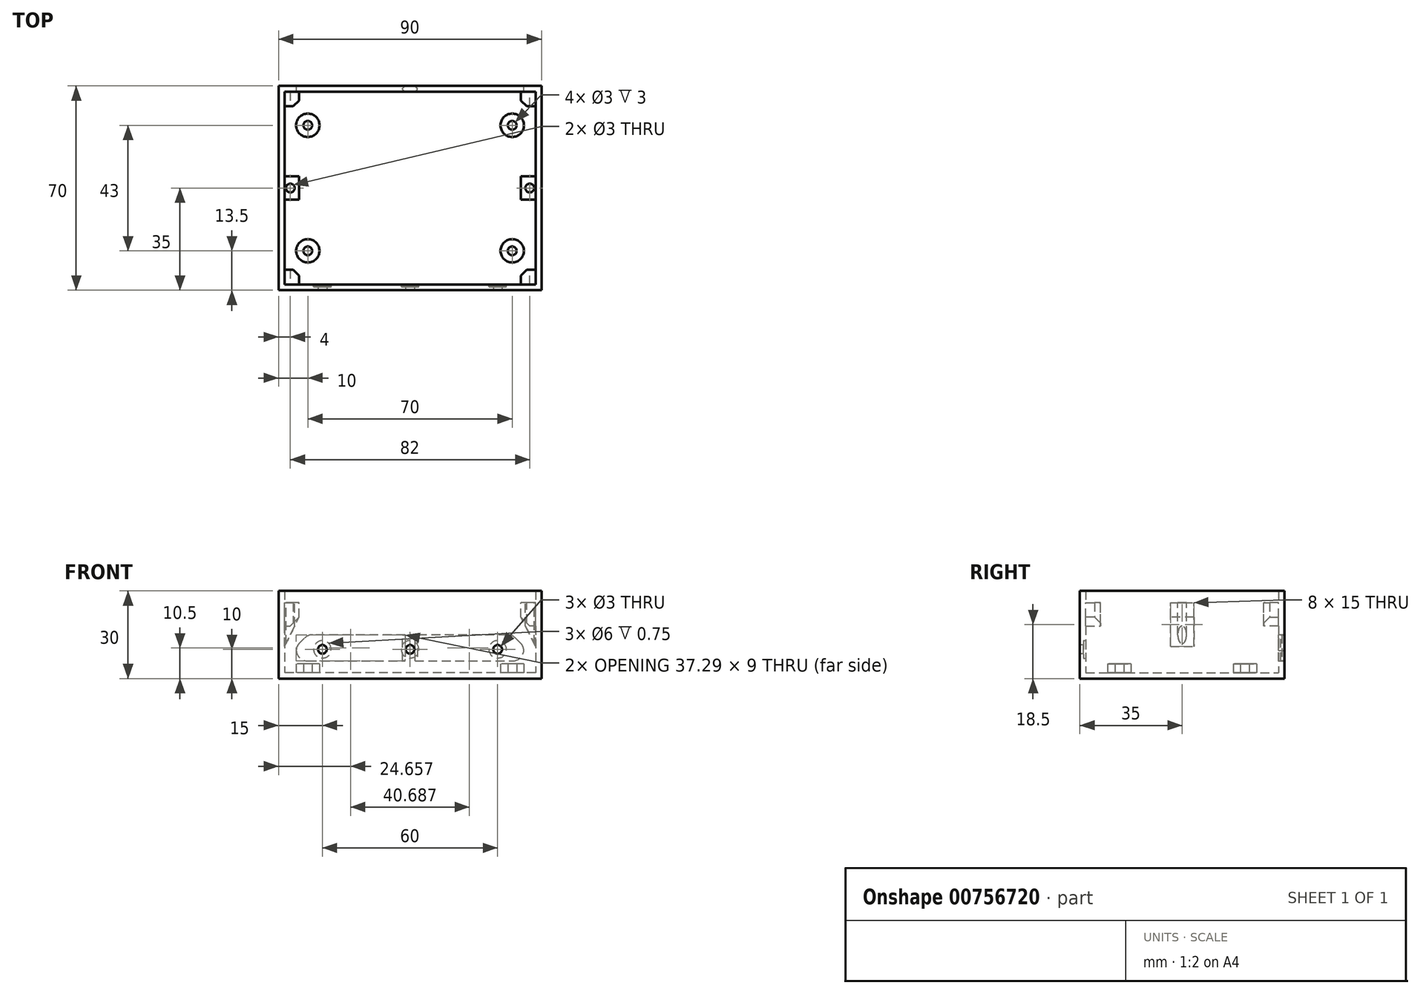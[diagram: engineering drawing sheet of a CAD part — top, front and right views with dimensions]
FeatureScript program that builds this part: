
annotation { "Feature Type Name" : "Feature", "Feature Type Description" : "" }
export const myFeature = defineFeature(function(context is Context, id is Id, definition is map)
    precondition{}
    {
        {
            var Q0;
            Q0=qCreatedBy(makeId("Top.planeOp"),FACE);
            var sketch = newSketch(context, id + "F0", { "sketchPlane" : qUnion([Q0])});
            skLineSegment(sketch, "E0.bottom", {"start": v(38.25, -25) * mm, "end": v(-38.25, -25) * mm, "construction": true});
            skLineSegment(sketch, "E0.top", {"start": v(38.25, 25) * mm, "end": v(-38.25, 25) * mm, "construction": true});
            skLineSegment(sketch, "E0.left", {"start": v(38.25, -25) * mm, "end": v(38.25, 25) * mm, "construction": true});
            skLineSegment(sketch, "E0.right", {"start": v(-38.25, -25) * mm, "end": v(-38.25, 25) * mm, "construction": true});
            skPoint(sketch, "E0.middle", {"position": v(0, 0) * mm});
            skPoint(sketch, "E1", {"position": v(35, 21.5) * mm});
            skPoint(sketch, "E2", {"position": v(-35, 21.5) * mm});
            skPoint(sketch, "E3", {"position": v(-35, -21.5) * mm});
            skPoint(sketch, "E4", {"position": v(35, -21.5) * mm});
            skLineSegment(sketch, "E5", {"start": v(35, 21.5) * mm, "end": v(-35, 21.5) * mm, "construction": true});
            skLineSegment(sketch, "E6", {"start": v(-35, -21.5) * mm, "end": v(35, -21.5) * mm, "construction": true});
            skLineSegment(sketch, "E7", {"start": v(35, 21.5) * mm, "end": v(35, -21.5) * mm, "construction": true});
            skLineSegment(sketch, "E8", {"start": v(-35, 21.5) * mm, "end": v(-35, -21.5) * mm, "construction": true});
            skCircle(sketch, "E9", {"center": v(-35, 21.5) * mm, "radius": 1.5 * mm});
            skCircle(sketch, "E10", {"center": v(35, 21.5) * mm, "radius": 1.5 * mm});
            skCircle(sketch, "E11", {"center": v(35, -21.5) * mm, "radius": 1.5 * mm});
            skCircle(sketch, "E12", {"center": v(-35, -21.5) * mm, "radius": 1.5 * mm});
            skLineSegment(sketch, "E13.bottom", {"start": v(45, -35) * mm, "end": v(-45, -35) * mm});
            skLineSegment(sketch, "E13.top", {"start": v(45, 35) * mm, "end": v(-45, 35) * mm});
            skLineSegment(sketch, "E13.left", {"start": v(45, -35) * mm, "end": v(45, 35) * mm});
            skLineSegment(sketch, "E13.right", {"start": v(-45, -35) * mm, "end": v(-45, 35) * mm});
            skLineSegment(sketch, "E14.bottom", {"start": v(43, -33) * mm, "end": v(-43, -33) * mm});
            skLineSegment(sketch, "E14.top", {"start": v(43, 33) * mm, "end": v(-43, 33) * mm});
            skLineSegment(sketch, "E14.left", {"start": v(43, -33) * mm, "end": v(43, 33) * mm});
            skLineSegment(sketch, "E14.right", {"start": v(-43, -33) * mm, "end": v(-43, 33) * mm});
            skCircle(sketch, "E15", {"center": v(-35, 21.5) * mm, "radius": 4 * mm});
            skCircle(sketch, "E16", {"center": v(35, 21.5) * mm, "radius": 4 * mm});
            skCircle(sketch, "E17", {"center": v(35, -21.5) * mm, "radius": 4 * mm});
            skCircle(sketch, "E18", {"center": v(-35, -21.5) * mm, "radius": 4 * mm});
            skSolve(sketch);
        }
        {
            var Q0;
            Q0=makeQuery(id+"F0.imprint","IMPRINT",FACE,{"disambiguationData":[TD([[makeQuery(id+"F0.imprint","IMPRINT",EDGE,{"derivedFrom":sQuery(id+"F0.wireOp",EDGE,"E9")}),-1.0]])]});
            var Q1;
            Q1=makeQuery(id+"F0.imprint","IMPRINT",FACE,{"disambiguationData":[TD([[makeQuery(id+"F0.imprint","IMPRINT",EDGE,{"derivedFrom":sQuery(id+"F0.wireOp",EDGE,"E10")}),-1.0]])]});
            var Q2;
            Q2=makeQuery(id+"F0.imprint","IMPRINT",FACE,{"disambiguationData":[TD([[makeQuery(id+"F0.imprint","IMPRINT",EDGE,{"derivedFrom":sQuery(id+"F0.wireOp",EDGE,"E11")}),-1.0]])]});
            var Q3;
            Q3=makeQuery(id+"F0.imprint","IMPRINT",FACE,{"disambiguationData":[TD([[makeQuery(id+"F0.imprint","IMPRINT",EDGE,{"derivedFrom":sQuery(id+"F0.wireOp",EDGE,"E12")}),-1.0]])]});
            extrude(context, id + "F1", {"entities" : qUnion([Q0, Q1, Q2, Q3]), "depth" : 5 * mm, "offsetDistance" : 25 * mm});
        }
        {
            var Q0;
            Q0=makeQuery(id+"F0.imprint","IMPRINT",FACE,{"disambiguationData":[TD([[makeQuery(id+"F0.imprint","IMPRINT",EDGE,{"derivedFrom":sQuery(id+"F0.wireOp",EDGE,"E9")}),-1.0]])]});
            var Q1;
            Q1=makeQuery(id+"F0.imprint","IMPRINT",FACE,{"disambiguationData":[TD([[makeQuery(id+"F0.imprint","IMPRINT",EDGE,{"derivedFrom":sQuery(id+"F0.wireOp",EDGE,"E14.bottom")}),-1.0]])]});
            var Q2;
            Q2=makeQuery(id+"F0.imprint","IMPRINT",FACE,{"disambiguationData":[TD([[makeQuery(id+"F0.imprint","IMPRINT",EDGE,{"derivedFrom":sQuery(id+"F0.wireOp",EDGE,"E10")}),1.0]])]});
            var Q3;
            Q3=makeQuery(id+"F0.imprint","IMPRINT",FACE,{"disambiguationData":[TD([[makeQuery(id+"F0.imprint","IMPRINT",EDGE,{"derivedFrom":sQuery(id+"F0.wireOp",EDGE,"E11")}),1.0]])]});
            var Q4;
            Q4=makeQuery(id+"F0.imprint","IMPRINT",FACE,{"disambiguationData":[TD([[makeQuery(id+"F0.imprint","IMPRINT",EDGE,{"derivedFrom":sQuery(id+"F0.wireOp",EDGE,"E12")}),1.0]])]});
            var Q5;
            Q5=makeQuery(id+"F0.imprint","IMPRINT",FACE,{"disambiguationData":[TD([[makeQuery(id+"F0.imprint","IMPRINT",EDGE,{"derivedFrom":sQuery(id+"F0.wireOp",EDGE,"E9")}),1.0]])]});
            extrude(context, id + "F2", {"entities" : qUnion([Q0, Q1, Q2, Q3, Q4, Q5]), "operationType" : NewBodyOperationType.ADD, "depth" : 2 * mm, "offsetDistance" : 25 * mm});
        }
        {
            var Q0;
            Q0=makeQuery(id+"F0.imprint","IMPRINT",FACE,{"disambiguationData":[TD([[makeQuery(id+"F0.imprint","IMPRINT",EDGE,{"derivedFrom":sQuery(id+"F0.wireOp",EDGE,"E13.bottom")}),-1.0]])]});
            extrude(context, id + "F3", {"entities" : qUnion([Q0]), "operationType" : NewBodyOperationType.ADD, "depth" : 30 * mm, "offsetDistance" : 25 * mm});
        }
        {
            var Q0;
            Q0=makeQuery(id+"F3.opExtrude","SWEPT_FACE",FACE,{"disambiguationData":[OSD([sQuery(id+"F0.wireOp",EDGE,"E13.bottom")])]});
            var sketch = newSketch(context, id + "F4", { "sketchPlane" : qUnion([Q0])});
            skLineSegment(sketch, "E19", {"start": v(-45, 10) * mm, "end": v(45, 10) * mm, "construction": true});
            skCircle(sketch, "E20", {"center": v(-30, 10) * mm, "radius": 1.5 * mm});
            skCircle(sketch, "E21.1.0.0", {"center": v(0, 10) * mm, "radius": 1.5 * mm});
            skCircle(sketch, "E21.2.0.0", {"center": v(30, 10) * mm, "radius": 1.5 * mm});
            skLineSegment(sketch, "E21.direction1", {"start": v(-30, 10) * mm, "end": v(0, 10) * mm, "construction": true});
            skCircle(sketch, "E22", {"center": v(-30, 10) * mm, "radius": 3 * mm});
            skCircle(sketch, "E23.1.0.0", {"center": v(0, 10) * mm, "radius": 3 * mm});
            skCircle(sketch, "E23.2.0.0", {"center": v(30, 10) * mm, "radius": 3 * mm});
            skSolve(sketch);
        }
        {
            var Q0;
            Q0=makeQuery(id+"F4.imprint","IMPRINT",FACE,{"disambiguationData":[TD([[makeQuery(id+"F4.imprint","IMPRINT",EDGE,{"derivedFrom":sQuery(id+"F4.wireOp",EDGE,"E20")}),1.0]])]});
            var Q1;
            Q1=makeQuery(id+"F4.imprint","IMPRINT",FACE,{"disambiguationData":[TD([[makeQuery(id+"F4.imprint","IMPRINT",EDGE,{"derivedFrom":sQuery(id+"F4.wireOp",EDGE,"E21.1.0.0")}),1.0]])]});
            var Q2;
            Q2=makeQuery(id+"F4.imprint","IMPRINT",FACE,{"disambiguationData":[TD([[makeQuery(id+"F4.imprint","IMPRINT",EDGE,{"derivedFrom":sQuery(id+"F4.wireOp",EDGE,"E21.2.0.0")}),1.0]])]});
            extrude(context, id + "F5", {"entities" : qUnion([Q0, Q1, Q2]), "operationType" : NewBodyOperationType.REMOVE, "endBound" : BoundingType.UP_TO_NEXT, "oppositeDirection" : true, "depth" : 25 * mm, "offsetDistance" : 25 * mm});
        }
        {
            var Q0;
            Q0=makeQuery(id+"F3.opExtrude","SWEPT_FACE",FACE,{"disambiguationData":[OSD([sQuery(id+"F0.wireOp",EDGE,"E14.bottom")])]});
            var sketch = newSketch(context, id + "F6", { "sketchPlane" : qUnion([Q0])});
            skCircle(sketch, "E24", {"center": v(-30, 10) * mm, "radius": 3 * mm});
            skCircle(sketch, "E25.1.0.0", {"center": v(0, 10) * mm, "radius": 3 * mm});
            skCircle(sketch, "E25.2.0.0", {"center": v(30, 10) * mm, "radius": 3 * mm});
            skLineSegment(sketch, "E25.direction1", {"start": v(-30, 10) * mm, "end": v(0, 10) * mm, "construction": true});
            skSolve(sketch);
        }
        {
            var Q0;
            Q0=makeQuery(id+"F6.imprint","IMPRINT",FACE,{"disambiguationData":[TD([[makeQuery(id+"F6.imprint","IMPRINT",EDGE,{"derivedFrom":sQuery(id+"F6.wireOp",EDGE,"E24")}),1.0]])]});
            var Q1;
            Q1=makeQuery(id+"F6.imprint","IMPRINT",FACE,{"disambiguationData":[TD([[makeQuery(id+"F6.imprint","IMPRINT",EDGE,{"derivedFrom":sQuery(id+"F6.wireOp",EDGE,"E25.1.0.0")}),1.0]])]});
            var Q2;
            Q2=makeQuery(id+"F6.imprint","IMPRINT",FACE,{"disambiguationData":[TD([[makeQuery(id+"F6.imprint","IMPRINT",EDGE,{"derivedFrom":sQuery(id+"F6.wireOp",EDGE,"E25.2.0.0")}),1.0]])]});
            extrude(context, id + "F7", {"entities" : qUnion([Q0, Q1, Q2]), "operationType" : NewBodyOperationType.REMOVE, "oppositeDirection" : true, "depth" : 0.75 * mm, "offsetDistance" : 25 * mm});
        }
        {
            var Q0;
            Q0=makeQuery(id+"F3.opExtrude","CAP_FACE",FACE,{"disambiguationData":[OSD([sQuery(id+"F0.wireOp",EDGE,"E13.bottom"),sQuery(id+"F0.wireOp",EDGE,"E13.top"),sQuery(id+"F0.wireOp",EDGE,"E13.left"),sQuery(id+"F0.wireOp",EDGE,"E13.right"),sQuery(id+"F0.wireOp",EDGE,"E14.bottom"),sQuery(id+"F0.wireOp",EDGE,"E14.top"),sQuery(id+"F0.wireOp",EDGE,"E14.left"),sQuery(id+"F0.wireOp",EDGE,"E14.right")])],"isStart":false});
            cPlane(context, id + "F8", {"entities" : qUnion([Q0]), "cplaneType" : CPlaneType.OFFSET, "offset" : 4 * mm, "oppositeDirection" : true, "width" : 150 * mm, "height" : 150 * mm});
        }
        {
            var Q0;
            Q0=qCreatedBy(id+"F8.planeOp",FACE);
            var sketch = newSketch(context, id + "F9", { "sketchPlane" : qUnion([Q0])});
            skLineSegment(sketch, "E26.bottom", {"start": v(43, -33) * mm, "end": v(38, -33) * mm});
            skLineSegment(sketch, "E26.top", {"start": v(43, -28) * mm, "end": v(38, -28) * mm});
            skLineSegment(sketch, "E26.left", {"start": v(43, -33) * mm, "end": v(43, -28) * mm});
            skLineSegment(sketch, "E26.right", {"start": v(38, -33) * mm, "end": v(38, -28) * mm});
            skLineSegment(sketch, "E27.bottom", {"start": v(-43, -33) * mm, "end": v(-38, -33) * mm});
            skLineSegment(sketch, "E27.top", {"start": v(-43, -28) * mm, "end": v(-38, -28) * mm});
            skLineSegment(sketch, "E27.left", {"start": v(-43, -33) * mm, "end": v(-43, -28) * mm});
            skLineSegment(sketch, "E27.right", {"start": v(-38, -33) * mm, "end": v(-38, -28) * mm});
            skLineSegment(sketch, "E28.bottom", {"start": v(-43, 33) * mm, "end": v(-38, 33) * mm});
            skLineSegment(sketch, "E28.top", {"start": v(-43, 28) * mm, "end": v(-38, 28) * mm});
            skLineSegment(sketch, "E28.left", {"start": v(-43, 33) * mm, "end": v(-43, 28) * mm});
            skLineSegment(sketch, "E28.right", {"start": v(-38, 33) * mm, "end": v(-38, 28) * mm});
            skLineSegment(sketch, "E29.bottom", {"start": v(43, 33) * mm, "end": v(38, 33) * mm});
            skLineSegment(sketch, "E29.top", {"start": v(43, 28) * mm, "end": v(38, 28) * mm});
            skLineSegment(sketch, "E29.left", {"start": v(43, 33) * mm, "end": v(43, 28) * mm});
            skLineSegment(sketch, "E29.right", {"start": v(38, 33) * mm, "end": v(38, 28) * mm});
            skLineSegment(sketch, "E30", {"start": v(-43, 0) * mm, "end": v(43, 0) * mm, "construction": true});
            skLineSegment(sketch, "E31.bottom", {"start": v(43, -4) * mm, "end": v(38, -4) * mm});
            skLineSegment(sketch, "E31.top", {"start": v(43, 4) * mm, "end": v(38, 4) * mm});
            skLineSegment(sketch, "E31.left", {"start": v(43, -4) * mm, "end": v(43, 4) * mm});
            skLineSegment(sketch, "E31.right", {"start": v(38, -4) * mm, "end": v(38, 4) * mm});
            skLineSegment(sketch, "E32.bottom", {"start": v(-43, -4) * mm, "end": v(-38, -4) * mm});
            skLineSegment(sketch, "E32.top", {"start": v(-43, 4) * mm, "end": v(-38, 4) * mm});
            skLineSegment(sketch, "E32.left", {"start": v(-43, -4) * mm, "end": v(-43, 4) * mm});
            skLineSegment(sketch, "E32.right", {"start": v(-38, -4) * mm, "end": v(-38, 4) * mm});
            skPoint(sketch, "E33", {"position": v(43, 0) * mm});
            skPoint(sketch, "E34", {"position": v(-43, 0) * mm});
            skPoint(sketch, "E35", {"position": v(41, 0) * mm});
            skPoint(sketch, "E36", {"position": v(-41, 0) * mm});
            skCircle(sketch, "E37", {"center": v(41, 0) * mm, "radius": 1.5 * mm});
            skCircle(sketch, "E38", {"center": v(-41, 0) * mm, "radius": 1.5 * mm});
            skSolve(sketch);
        }
        {
            var Q0;
            Q0=makeQuery(id+"F9.imprint","IMPRINT",FACE,{"disambiguationData":[TD([[makeQuery(id+"F9.imprint","IMPRINT",EDGE,{"derivedFrom":sQuery(id+"F9.wireOp",EDGE,"E26.bottom")}),-1.0]])]});
            var Q1;
            Q1=makeQuery(id+"F9.imprint","IMPRINT",FACE,{"disambiguationData":[TD([[makeQuery(id+"F9.imprint","IMPRINT",EDGE,{"derivedFrom":sQuery(id+"F9.wireOp",EDGE,"E29.bottom")}),1.0]])]});
            var Q2;
            Q2=makeQuery(id+"F9.imprint","IMPRINT",FACE,{"disambiguationData":[TD([[makeQuery(id+"F9.imprint","IMPRINT",EDGE,{"derivedFrom":sQuery(id+"F9.wireOp",EDGE,"E27.bottom")}),1.0]])]});
            var Q3;
            Q3=makeQuery(id+"F9.imprint","IMPRINT",FACE,{"disambiguationData":[TD([[makeQuery(id+"F9.imprint","IMPRINT",EDGE,{"derivedFrom":sQuery(id+"F9.wireOp",EDGE,"E28.bottom")}),-1.0]])]});
            extrude(context, id + "F10", {"entities" : qUnion([Q0, Q1, Q2, Q3]), "operationType" : NewBodyOperationType.ADD, "oppositeDirection" : true, "depth" : 8 * mm, "offsetDistance" : 25 * mm});
        }
        {
            var Q0;
            Q0=makeQuery(id+"F10.opExtrude","CAP_EDGE",EDGE,{"disambiguationData":[OSD([sQuery(id+"F9.wireOp",EDGE,"E27.right")])],"isStart":false});
            var Q1;
            Q1=makeQuery(id+"F10.opExtrude","CAP_EDGE",EDGE,{"disambiguationData":[OSD([sQuery(id+"F9.wireOp",EDGE,"E28.right")])],"isStart":false});
            var Q2;
            Q2=makeQuery(id+"F10.opExtrude","CAP_EDGE",EDGE,{"disambiguationData":[OSD([sQuery(id+"F9.wireOp",EDGE,"E26.right")])],"isStart":false});
            var Q3;
            Q3=makeQuery(id+"F10.opExtrude","CAP_EDGE",EDGE,{"disambiguationData":[OSD([sQuery(id+"F9.wireOp",EDGE,"E29.right")])],"isStart":false});
            chamfer(context, id + "F11", {"entities" : qUnion([Q0, Q1, Q2, Q3]), "width" : 3 * mm, "tangentPropagation" : true});
        }
        {
            var Q0;
            Q0=makeQuery(id+"F10.opExtrude","SWEPT_EDGE",EDGE,{"disambiguationData":[OSD([sQuery(id+"F9.wireOp",EDGE,"E28.top"),sQuery(id+"F9.wireOp",EDGE,"E28.right")])]});
            var Q1;
            Q1=makeQuery(id+"F10.opExtrude","SWEPT_EDGE",EDGE,{"disambiguationData":[OSD([sQuery(id+"F9.wireOp",EDGE,"E27.top"),sQuery(id+"F9.wireOp",EDGE,"E27.right")])]});
            var Q2;
            Q2=makeQuery(id+"F10.opExtrude","SWEPT_EDGE",EDGE,{"disambiguationData":[OSD([sQuery(id+"F9.wireOp",EDGE,"E26.top"),sQuery(id+"F9.wireOp",EDGE,"E26.right")])]});
            var Q3;
            Q3=makeQuery(id+"F10.opExtrude","SWEPT_EDGE",EDGE,{"disambiguationData":[OSD([sQuery(id+"F9.wireOp",EDGE,"E29.top"),sQuery(id+"F9.wireOp",EDGE,"E29.right")])]});
            chamfer(context, id + "F12", {"entities" : qUnion([Q0, Q1, Q2, Q3]), "width" : 2 * mm, "tangentPropagation" : true});
        }
        {
            var Q0;
            Q0=makeQuery(id+"F3.opExtrude","SWEPT_FACE",FACE,{"disambiguationData":[OSD([sQuery(id+"F0.wireOp",EDGE,"E13.top")])]});
            var sketch = newSketch(context, id + "F13", { "sketchPlane" : qUnion([Q0])});
            skLineSegment(sketch, "E39", {"start": v(-45, 15) * mm, "end": v(45, 15) * mm});
            skLineSegment(sketch, "E40", {"start": v(45, 6) * mm, "end": v(-45, 6) * mm});
            skLineSegment(sketch, "E41", {"start": v(39, 15) * mm, "end": v(39, 6) * mm});
            skLineSegment(sketch, "E42", {"start": v(-39, 15) * mm, "end": v(-39, 6) * mm});
            skSolve(sketch);
        }
        {
            var Q0;
            {var subQ0=sQuery(id+"F13.wireOp",EDGE,"E41");Q0=makeQuery(id+"F13.imprint","IMPRINT",FACE,{"disambiguationData":[TD([[makeQuery(id+"F13.imprint","IMPRINT",EDGE,{"derivedFrom":subQ0}),-1.0]])]});}
            extrude(context, id + "F14", {"entities" : qUnion([Q0]), "operationType" : NewBodyOperationType.REMOVE, "endBound" : BoundingType.UP_TO_NEXT, "oppositeDirection" : true, "depth" : 25 * mm, "offsetDistance" : 25 * mm});
        }
        {
            var Q0;
            Q0=makeQuery(id+"F14.boolean.opBoolean","COPY",EDGE,{"derivedFrom":makeQuery(id+"F14.opExtrude","SWEPT_EDGE",EDGE,{"disambiguationData":[OSD([sQuery(id+"F13.wireOp",EDGE,"E39"),sQuery(id+"F13.wireOp",EDGE,"E41")])]})});
            var Q1;
            Q1=makeQuery(id+"F14.boolean.opBoolean","COPY",EDGE,{"derivedFrom":makeQuery(id+"F14.opExtrude","SWEPT_EDGE",EDGE,{"disambiguationData":[OSD([sQuery(id+"F13.wireOp",EDGE,"E39"),sQuery(id+"F13.wireOp",EDGE,"E42")])]})});
            chamfer(context, id + "F15", {"entities" : qUnion([Q0, Q1]), "width" : 4 * mm, "tangentPropagation" : true});
        }
        {
            var Q0;
            Q0=makeQuery(id+"F14.boolean.opBoolean","COPY",EDGE,{"derivedFrom":makeQuery(id+"F14.opExtrude","SWEPT_EDGE",EDGE,{"disambiguationData":[OSD([sQuery(id+"F13.wireOp",EDGE,"E40"),sQuery(id+"F13.wireOp",EDGE,"E41")])]})});
            var Q1;
            Q1=makeQuery(id+"F14.boolean.opBoolean","COPY",EDGE,{"derivedFrom":makeQuery(id+"F14.opExtrude","SWEPT_EDGE",EDGE,{"disambiguationData":[OSD([sQuery(id+"F13.wireOp",EDGE,"E40"),sQuery(id+"F13.wireOp",EDGE,"E42")])]})});
            var Q2;
            {var subQ0=sQuery(id+"F13.wireOp",EDGE,"E39");Q2=makeQuery(id+"F15.opChamfer","BLEND_EDGE",EDGE,{"blendedFrom":[makeQuery(id+"F14.boolean.opBoolean","COPY",EDGE,{"derivedFrom":makeQuery(id+"F14.opExtrude","SWEPT_EDGE",EDGE,{"disambiguationData":[OSD([subQ0,sQuery(id+"F13.wireOp",EDGE,"E41")])]})}),makeQuery(id+"F14.boolean.opBoolean","COPY",FACE,{"derivedFrom":makeQuery(id+"F14.opExtrude","SWEPT_FACE",FACE,{"disambiguationData":[OSD([subQ0])]})})],"blendedInto":[makeQuery(id+"F14.boolean.opBoolean","COPY",FACE,{"derivedFrom":makeQuery(id+"F14.opExtrude","SWEPT_FACE",FACE,{"disambiguationData":[OSD([subQ0])]})})]});}
            var Q3;
            {var subQ0=sQuery(id+"F13.wireOp",EDGE,"E39");Q3=makeQuery(id+"F15.opChamfer","BLEND_EDGE",EDGE,{"blendedFrom":[makeQuery(id+"F14.boolean.opBoolean","COPY",EDGE,{"derivedFrom":makeQuery(id+"F14.opExtrude","SWEPT_EDGE",EDGE,{"disambiguationData":[OSD([subQ0,sQuery(id+"F13.wireOp",EDGE,"E42")])]})}),makeQuery(id+"F14.boolean.opBoolean","COPY",FACE,{"derivedFrom":makeQuery(id+"F14.opExtrude","SWEPT_FACE",FACE,{"disambiguationData":[OSD([subQ0])]})})],"blendedInto":[makeQuery(id+"F14.boolean.opBoolean","COPY",FACE,{"derivedFrom":makeQuery(id+"F14.opExtrude","SWEPT_FACE",FACE,{"disambiguationData":[OSD([subQ0])]})})]});}
            var Q4;
            {var subQ0=sQuery(id+"F13.wireOp",EDGE,"E41");Q4=makeQuery(id+"F15.opChamfer","BLEND_EDGE",EDGE,{"blendedFrom":[makeQuery(id+"F14.boolean.opBoolean","COPY",EDGE,{"derivedFrom":makeQuery(id+"F14.opExtrude","SWEPT_EDGE",EDGE,{"disambiguationData":[OSD([sQuery(id+"F13.wireOp",EDGE,"E39"),subQ0])]})}),makeQuery(id+"F14.boolean.opBoolean","COPY",FACE,{"derivedFrom":makeQuery(id+"F14.opExtrude","SWEPT_FACE",FACE,{"disambiguationData":[OSD([subQ0])]})})],"blendedInto":[makeQuery(id+"F14.boolean.opBoolean","COPY",FACE,{"derivedFrom":makeQuery(id+"F14.opExtrude","SWEPT_FACE",FACE,{"disambiguationData":[OSD([subQ0])]})})]});}
            var Q5;
            {var subQ0=sQuery(id+"F13.wireOp",EDGE,"E42");Q5=makeQuery(id+"F15.opChamfer","BLEND_EDGE",EDGE,{"blendedFrom":[makeQuery(id+"F14.boolean.opBoolean","COPY",EDGE,{"derivedFrom":makeQuery(id+"F14.opExtrude","SWEPT_EDGE",EDGE,{"disambiguationData":[OSD([sQuery(id+"F13.wireOp",EDGE,"E39"),subQ0])]})}),makeQuery(id+"F14.boolean.opBoolean","COPY",FACE,{"derivedFrom":makeQuery(id+"F14.opExtrude","SWEPT_FACE",FACE,{"disambiguationData":[OSD([subQ0])]})})],"blendedInto":[makeQuery(id+"F14.boolean.opBoolean","COPY",FACE,{"derivedFrom":makeQuery(id+"F14.opExtrude","SWEPT_FACE",FACE,{"disambiguationData":[OSD([subQ0])]})})]});}
            fillet(context, id + "F16", {"entities" : qUnion([Q0, Q1, Q2, Q3, Q4, Q5]), "radius" : 4 * mm, "tangentPropagation" : true, "allowEdgeOverflow" : false});
        }
        {
            var Q0;
            Q0=makeQuery(id+"F14.boolean.opBoolean","COPY",FACE,{"derivedFrom":makeQuery(id+"F14.opExtrude","SWEPT_FACE",FACE,{"disambiguationData":[OSD([sQuery(id+"F13.wireOp",EDGE,"E39")])]})});
            var sketch = newSketch(context, id + "F17", { "sketchPlane" : qUnion([Q0])});
            skLineSegment(sketch, "E43", {"start": v(0, -33) * mm, "end": v(0, -35) * mm, "construction": true});
            skLineSegment(sketch, "E44", {"start": v(2.5, -33) * mm, "end": v(2.5, -35) * mm});
            skLineSegment(sketch, "E45", {"start": v(-2.5, -33) * mm, "end": v(-2.5, -35) * mm});
            skLineSegment(sketch, "E46", {"start": v(-2.5, -35) * mm, "end": v(2.5, -35) * mm, "construction": true});
            skSolve(sketch);
        }
        {
            var Q0;
            {var subQ0=sQuery(id+"F17.wireOp",EDGE,"E44");Q0=makeQuery(id+"F17.imprint","IMPRINT",FACE,{"disambiguationData":[TD([[makeQuery(id+"F17.imprint","IMPRINT",EDGE,{"derivedFrom":subQ0}),-1.0]])]});}
            var Q1;
            Q1=makeQuery(id+"F14.boolean.opBoolean","COPY",FACE,{"derivedFrom":makeQuery(id+"F14.opExtrude","SWEPT_FACE",FACE,{"disambiguationData":[OSD([sQuery(id+"F13.wireOp",EDGE,"E40")])]})});
            extrude(context, id + "F18", {"entities" : qUnion([Q0]), "operationType" : NewBodyOperationType.ADD, "endBound" : BoundingType.UP_TO_SURFACE, "depth" : 25 * mm, "endBoundEntityFace" : qUnion([Q1]), "offsetDistance" : 25 * mm});
        }
        {
            var Q0;
            {var subQ0=sQuery(id+"F17.wireOp",EDGE,"E44");var subQ1=sQuery(id+"F13.wireOp",EDGE,"E39");Q0=makeQuery(id+"F18.opExtrude","SWEPT_EDGE",EDGE,{"disambiguationData":[OSD([subQ1,subQ0]),TDD([makeQuery(id+"F17.imprint","INTERSECT",VERTEX,{"derivedFrom":[makeQuery(id+"F14.boolean.opBoolean","COPY",EDGE,{"derivedFrom":makeQuery(id+"F14.opExtrude","CAP_EDGE",EDGE,{"disambiguationData":[OSD([subQ1])],"isStart":true})}),subQ0]})])]});}
            var Q1;
            {var subQ0=sQuery(id+"F17.wireOp",EDGE,"E45");var subQ1=sQuery(id+"F13.wireOp",EDGE,"E39");Q1=makeQuery(id+"F18.opExtrude","SWEPT_EDGE",EDGE,{"disambiguationData":[OSD([subQ1,subQ0]),TDD([makeQuery(id+"F17.imprint","INTERSECT",VERTEX,{"derivedFrom":[makeQuery(id+"F14.boolean.opBoolean","COPY",EDGE,{"derivedFrom":makeQuery(id+"F14.opExtrude","CAP_EDGE",EDGE,{"disambiguationData":[OSD([subQ1])],"isStart":true})}),subQ0]})])]});}
            var Q2;
            {var subQ0=sQuery(id+"F17.wireOp",EDGE,"E44");var subQ1=sQuery(id+"F13.wireOp",EDGE,"E39");Q2=makeQuery(id+"F18.opExtrude","SWEPT_EDGE",EDGE,{"disambiguationData":[OSD([subQ1,subQ0]),TDD([makeQuery(id+"F17.imprint","INTERSECT",VERTEX,{"derivedFrom":[makeQuery(id+"F14.boolean.opBoolean","COPY",EDGE,{"derivedFrom":makeQuery(id+"F14.opExtrude","CAP_EDGE",EDGE,{"disambiguationData":[OSD([subQ1])],"isStart":false})}),subQ0]})])]});}
            var Q3;
            {var subQ0=sQuery(id+"F17.wireOp",EDGE,"E45");var subQ1=sQuery(id+"F13.wireOp",EDGE,"E39");Q3=makeQuery(id+"F18.opExtrude","SWEPT_EDGE",EDGE,{"disambiguationData":[OSD([subQ1,subQ0]),TDD([makeQuery(id+"F17.imprint","INTERSECT",VERTEX,{"derivedFrom":[makeQuery(id+"F14.boolean.opBoolean","COPY",EDGE,{"derivedFrom":makeQuery(id+"F14.opExtrude","CAP_EDGE",EDGE,{"disambiguationData":[OSD([subQ1])],"isStart":false})}),subQ0]})])]});}
            chamfer(context, id + "F19", {"entities" : qUnion([Q0, Q1, Q2, Q3]), "width" : 0.8 * mm, "tangentPropagation" : true});
        }
        {
            var Q0;
            {var subQ4=sQuery(id+"F9.wireOp",EDGE,"E32.bottom");Q0=makeQuery(id+"F9.imprint","IMPRINT",FACE,{"disambiguationData":[TD([[makeQuery(id+"F9.imprint","IMPRINT",EDGE,{"derivedFrom":subQ4}),1.0]])]});}
            var Q1;
            {var subQ4=sQuery(id+"F9.wireOp",EDGE,"E31.bottom");Q1=makeQuery(id+"F9.imprint","IMPRINT",FACE,{"disambiguationData":[TD([[makeQuery(id+"F9.imprint","IMPRINT",EDGE,{"derivedFrom":subQ4}),-1.0]])]});}
            extrude(context, id + "F20", {"entities" : qUnion([Q0, Q1]), "operationType" : NewBodyOperationType.ADD, "oppositeDirection" : true, "depth" : 15 * mm, "offsetDistance" : 25 * mm});
        }
        {
            var Q0;
            Q0=makeQuery(id+"F20.opExtrude","CAP_EDGE",EDGE,{"disambiguationData":[OSD([sQuery(id+"F9.wireOp",EDGE,"E31.right")])],"isStart":false});
            chamfer(context, id + "F21", {"entities" : qUnion([Q0]), "chamferType" : ChamferType.TWO_OFFSETS, "width1" : 5 * mm, "oppositeDirection" : false, "width2" : 10 * mm, "tangentPropagation" : true});
        }
        {
            var Q0;
            Q0=makeQuery(id+"F20.opExtrude","CAP_EDGE",EDGE,{"disambiguationData":[OSD([sQuery(id+"F9.wireOp",EDGE,"E32.right")])],"isStart":false});
            chamfer(context, id + "F22", {"entities" : qUnion([Q0]), "chamferType" : ChamferType.TWO_OFFSETS, "width1" : 10 * mm, "oppositeDirection" : false, "width2" : 5 * mm, "tangentPropagation" : true});
        }
    });
